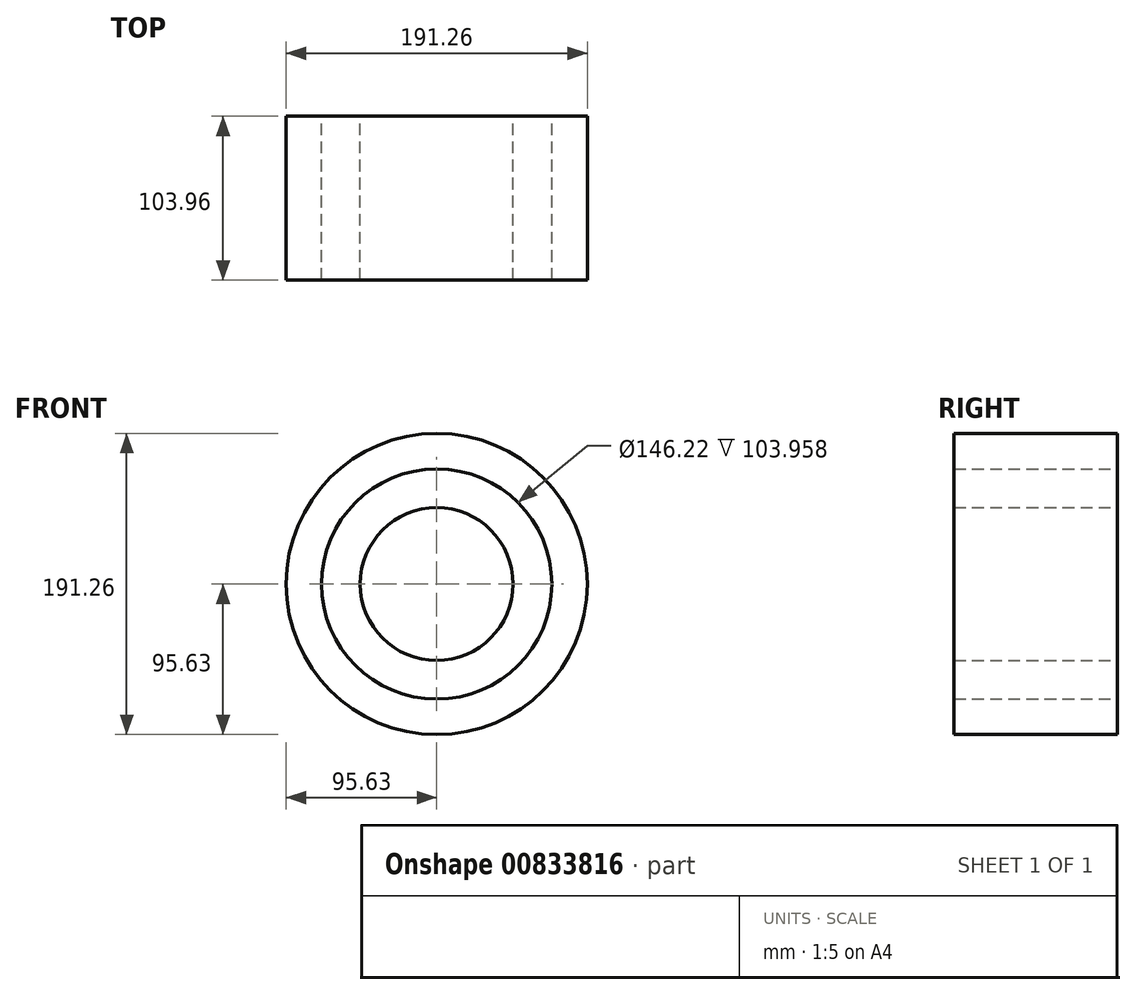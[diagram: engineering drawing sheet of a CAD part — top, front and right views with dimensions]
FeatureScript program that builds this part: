
annotation { "Feature Type Name" : "Feature", "Feature Type Description" : "" }
export const myFeature = defineFeature(function(context is Context, id is Id, definition is map)
    precondition{}
    {
        {
            var Q0;
            Q0=qCreatedBy(makeId("Front.planeOp"),FACE);
            var sketch = newSketch(context, id + "F0", { "sketchPlane" : qUnion([Q0])});
            skCircle(sketch, "E0", {"center": v(0, 0) * mm, "radius": 48.56 * mm});
            skCircle(sketch, "E1", {"center": v(0, 0) * mm, "radius": 73.1 * mm});
            skCircle(sketch, "E2", {"center": v(0, 0) * mm, "radius": 95.63 * mm});
            skSolve(sketch);
        }
        {
            var Q0;
            Q0=makeQuery(id+"F0.imprint","IMPRINT",FACE,{"disambiguationData":[TD([[makeQuery(id+"F0.imprint","IMPRINT",EDGE,{"derivedFrom":sQuery(id+"F0.wireOp",EDGE,"E1")}),-1.0]])]});
            var Q1;
            Q1=makeQuery(id+"F0.imprint","IMPRINT",FACE,{"disambiguationData":[TD([[makeQuery(id+"F0.imprint","IMPRINT",EDGE,{"derivedFrom":sQuery(id+"F0.wireOp",EDGE,"E0")}),1.0]])]});
            extrude(context, id + "F1", {"entities" : qUnion([Q0, Q1]), "depth" : 103.96 * mm, "offsetDistance" : 25 * mm});
        }
    });
